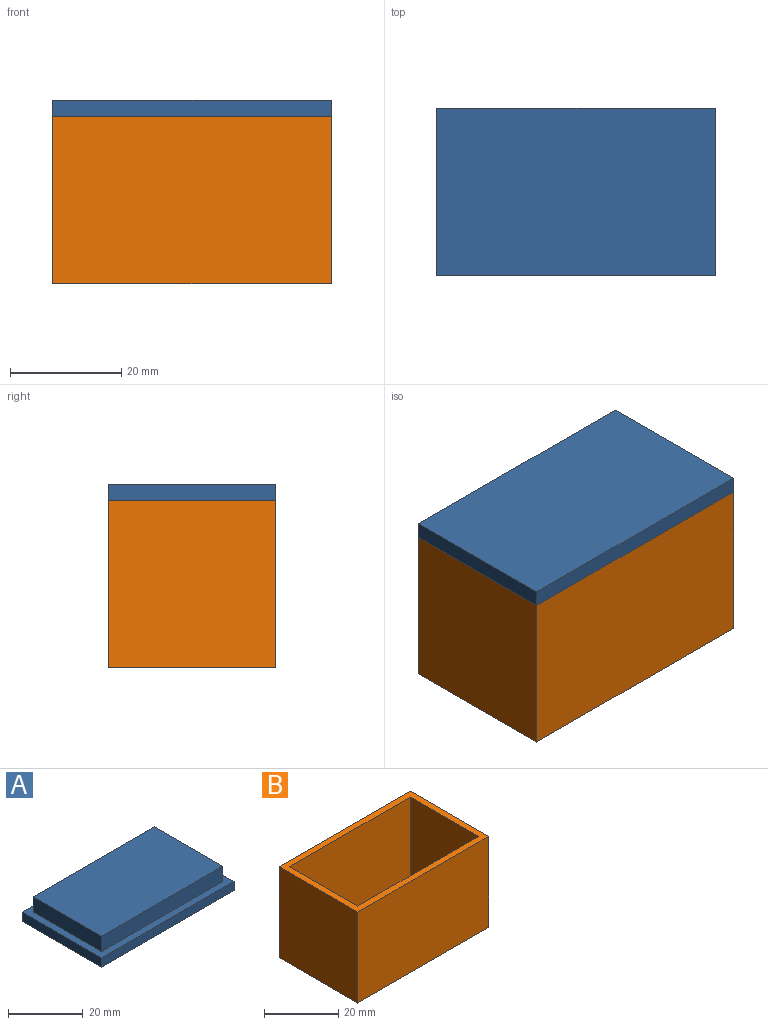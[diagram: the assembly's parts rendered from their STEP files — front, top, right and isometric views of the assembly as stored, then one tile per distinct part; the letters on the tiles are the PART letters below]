
ASSEMBLY  parts=2 mates=1
PART A: 11 faces, bbox 50x30x8 mm
  f0: plane 50x3mm, normal (0,-1,0), area 150mm2, adj f1,f3,f4,f5
  f1: plane 30x3mm, normal (1,0,0), area 90mm2, adj f0,f2,f4,f5
  f2: plane 50x3mm, normal (0,1,0), area 150mm2, adj f1,f3,f4,f5
  f3: plane 30x3mm, normal (-1,0,0), area 90mm2, adj f0,f2,f4,f5
  f4: plane 50x30mm, normal (0,0,1), area 318.4mm2, adj f0,f1,f2,f3,f6,f7,f8,f9
  f5: plane 50x30mm, normal (0,0,-1), area 1500mm2, adj f0,f1,f2,f3
  f6: plane 45.8x5mm, normal (0,-1,0), area 229mm2, adj f4,f7,f9,f10
  f7: plane 25.8x5mm, normal (1,0,0), area 129mm2, adj f4,f6,f8,f10
  f8: plane 45.8x5mm, normal (0,1,0), area 229mm2, adj f4,f7,f9,f10
  f9: plane 25.8x5mm, normal (-1,0,0), area 129mm2, adj f4,f6,f8,f10
  f10: plane 45.8x25.8mm, normal (0,0,1), area 1181.6mm2, adj f6,f7,f8,f9
PART B: 11 faces, bbox 50x30x30 mm
  f0: plane 50x30mm, normal (0,0,1), area 304mm2, adj f1,f2,f3,f4,f6,f7,f8,f9
  f1: plane 50x30mm, normal (0,-1,0), area 1500mm2, adj f0,f2,f4,f5
  f2: plane 30x30mm, normal (1,0,0), area 900mm2, adj f0,f1,f3,f5
  f3: plane 50x30mm, normal (0,1,0), area 1500mm2, adj f0,f2,f4,f5
  f4: plane 30x30mm, normal (-1,0,0), area 900mm2, adj f0,f1,f3,f5
  f5: plane 50x30mm, normal (0,0,-1), area 1500mm2, adj f1,f2,f3,f4
  f6: plane 46x28mm, normal (0,1,0), area 1288mm2, adj f0,f7,f9,f10
  f7: plane 28x26mm, normal (-1,0,0), area 728mm2, adj f0,f6,f8,f10
  f8: plane 46x28mm, normal (0,-1,0), area 1288mm2, adj f0,f7,f9,f10
  f9: plane 28x26mm, normal (1,0,0), area 728mm2, adj f0,f6,f8,f10
  f10: plane 46x26mm, normal (0,0,1), area 1196mm2, adj f6,f7,f8,f9
PLACE A rot(axis=(1,0,0),180deg) t=(-15.53,-1.68,28.92)mm
PLACE B t=(-15.53,-1.68,-4.08)mm
MATE fastened A.f4 <-> B.f0  axis (0,0,-1) through (-15.53,-1.68,25.92)mm
